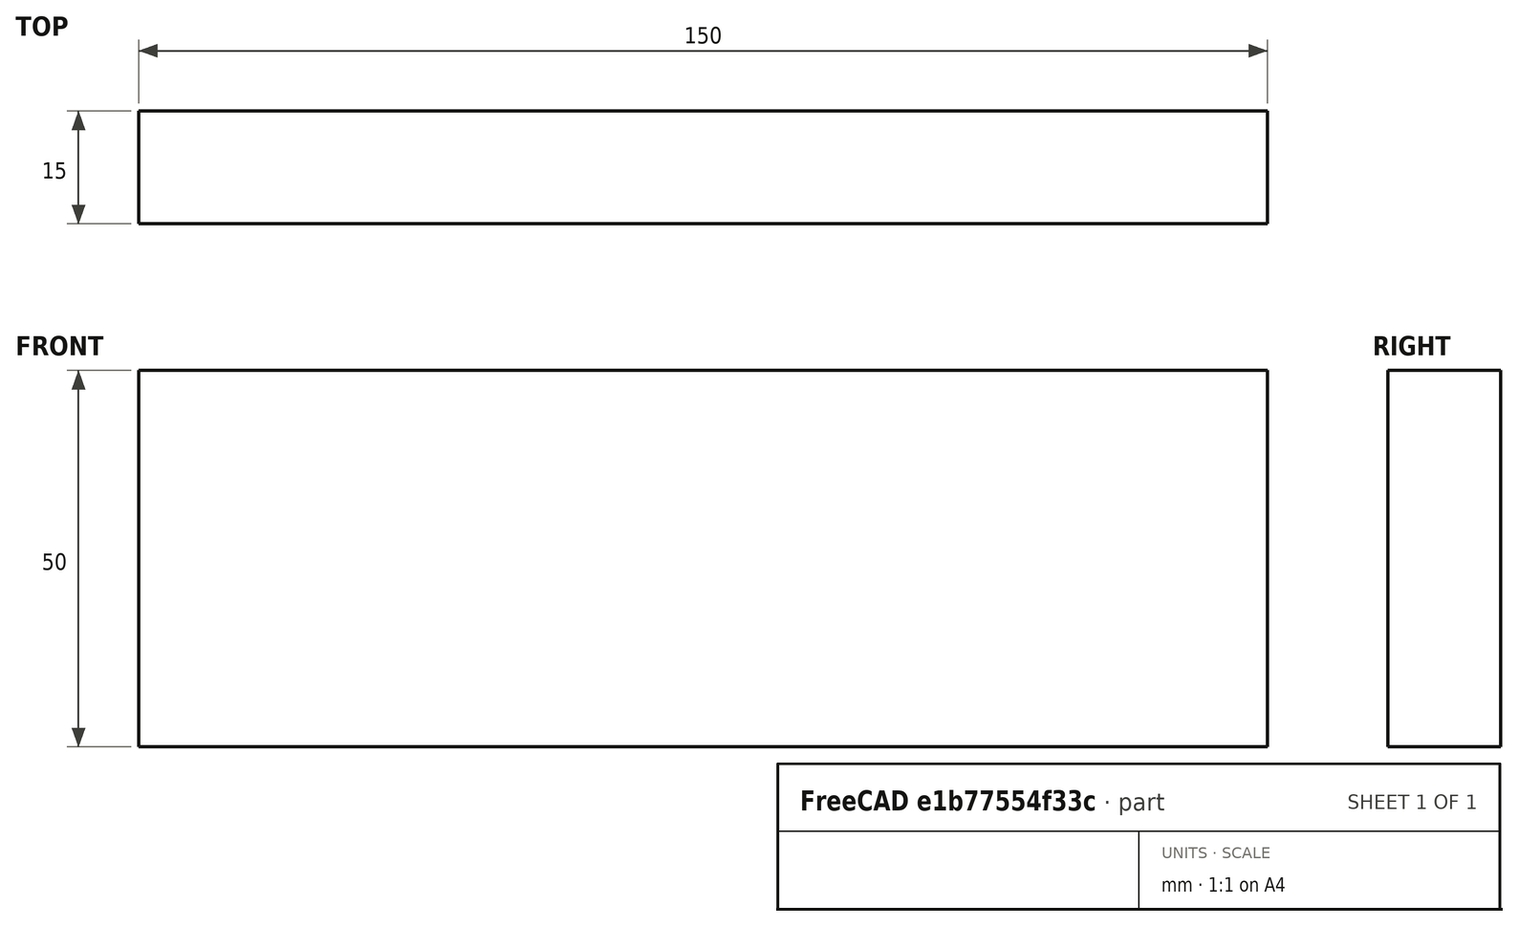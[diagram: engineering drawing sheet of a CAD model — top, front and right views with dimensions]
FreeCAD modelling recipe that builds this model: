
FCSTD DOCUMENT  (FreeCAD 0.15R4671 (Git))
Label: Flat Bar 150x15 EN10058 S235JR
License: All rights reserved
LicenseURL: http://en.wikipedia.org/wiki/All_rights_reserved
objects: Sketcher::SketchObject×1, Part::Extrusion×1
note: 2 computed .brp shape members not serialized (recipe doc carries the construction recipe); baked Part::Feature solids carry a one-line shape summary decoded from their .brp

FEATURE [Sketcher::SketchObject] Sketch
  sketch-geometry (4):
    g0: LineSegment StartX=-75 StartY=-7.5 StartZ=0 EndX=75 EndY=-7.5 EndZ=0
    g1: LineSegment StartX=75 StartY=-7.5 StartZ=0 EndX=75 EndY=7.5 EndZ=0
    g2: LineSegment StartX=75 StartY=7.5 StartZ=0 EndX=-75 EndY=7.5 EndZ=0
    g3: LineSegment StartX=-75 StartY=7.5 StartZ=0 EndX=-75 EndY=-7.5 EndZ=0
  constraints (12):
    c: Coincident(g0,g1)
    c: Coincident(g1,g2)
    c: Coincident(g2,g3)
    c: Coincident(g3,g0)
    c: Horizontal(g0)
    c: Horizontal(g2)
    c: Vertical(g1)
    c: Vertical(g3)
    c: Symmetric(g1,g2,g-2)
    c: Symmetric(g0,g1,g-1)
    c: DistanceY(g1) = 15
    c: DistanceX(g0) = 150
FEATURE [Part::Extrusion] Extrude  label="Flat Bar 150x15 EN10058 S235JR"
  Base = -> Sketch
  Dir = (0,0,50)
  Solid = true
